# Revit family: Selector Valve Solenoid Bracket-JCI_Sapphire_Plus-(70bar)Novec1230
name_source: partatom
category: Specialty Equipment
revit_build: Autodesk Revit 2017 (Build: 20171027_0315(x64)
units: mm (PartAtom-declared; Revit-internal decimal feet)

## family parameters
Always vertical = No
Cut with Voids When Loaded = No
OmniClass Number = 23.29.33.13.11
Part Type = Normal
Room Calculation Point = No
Round Connector Dimension = Use Diameter
Shared = No
Work Plane-Based = Yes

## types (3) — shared parameters
Connection Holes = 6 mm  [stored 0.019685 ft]
Date Modified = YYYY/MM/DD
Discharge Flow = 0 GPM
Family Version = 1.0
Fire Suppression Agent = ''3M Novec'' 1230 Fire Protection Fluid
Hole Diameter = 13 mm
Manufacturer = Johnson Controls, Inc.
Material = JCI - Iron - Gray
Model Disclaimer = For More Information Contact JOHNSON CONTROLS
Operating Temperature = 122 °F
Product Documentation Link = http://www.sapphireplus.com
Product Material = JCI - Iron - Gray
Product Page URL = http://www.sapphireplus.com
URL = http://www.sapphireplus.com
Unit Assembly = Sapphire Plus_Solenoid Bracket Assembly
Weight = 0.00 lbf
zero-valued in all types: Default Elevation

## per-type parameters (varying)
| type | Description | Equipment Abbreviation | Number of Holes | Perfil | Perfil Length | Solenoid Bracket Type |
| 30650022 | Selector valve solenoid mounting bracket_2 Solenoids |  | 2 | 330 mm  [stored 1.08268 ft] | 280 mm  [stored 0.918635 ft] | 2 |
| 30650013 | Selector valve solenoid mounting bracket_3 Solenoids | XXX | 3 | 475 mm  [stored 1.5584 ft] | 425 mm  [stored 1.39436 ft] | 3 |
| 30650014 | Selector valve solenoid mounting bracket_4 Solenoids |  | 4 | 620 mm  [stored 2.03412 ft] | 570 mm  [stored 1.87008 ft] | 4 |

note: column(s) folded — value = type name in every type: Model

note: [stored X ft] marks values corroborated as IEEE doubles in the binary element streams (Revit-internal decimal feet)

## geometry (parser evidence)
native form markers: Sweep x2
no freeform markers — native parametric forms only
